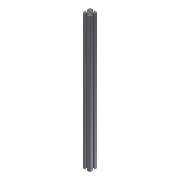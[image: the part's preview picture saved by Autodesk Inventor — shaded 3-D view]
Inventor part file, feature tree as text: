
AUTODESK INVENTOR PART (.ipt)
format: ipt  version: 2016 (Build 200138000, 138)  size: 182,784 bytes
history: native  units: mm
features: other x42, sketch x5, hole x4, extrude x1
ambient origin geometry x8: Origin, YZ Plane, XZ Plane, XY Plane, X Axis, Y Axis, Z Axis, Center Point
bodies: Solid1 (feature_tree)
feature tree (52):
  extrude  "Extrusion1"  [1 undecoded]
  hole  "Drilling 1"  [1 undecoded]
  hole  "Drilling 2"  [1 undecoded]
  hole  "Drilling 3"  [1 undecoded]
  hole  "Drilling 4"  [1 undecoded]
  other  "side_4d_XY"
  other  "side_4d_YZ"
  other  "side_4d_ZX"
  other  "side_4d_X"
  other  "side_4d_Y"
  other  "side_4d_Z"
  other  "side_4d_Center"
  other  "side_1a_XY"
  other  "side_1a_YZ"
  other  "side_1a_ZX"
  other  "side_1a_X"
  other  "side_1a_Y"
  other  "side_1a_Z"
  other  "side_1a_Center"
  other  "side_2b_XY"
  other  "side_2b_YZ"
  other  "side_2b_ZX"
  other  "side_2b_X"
  other  "side_2b_Y"
  other  "side_2b_Z"
  other  "side_2b_Center"
  other  "side_3c_XY"
  other  "side_3c_YZ"
  other  "side_3c_ZX"
  other  "side_3c_X"
  other  "side_3c_Y"
  other  "side_3c_Z"
  other  "side_3c_Center"
  other  "end_XY"
  other  "end_YZ"
  other  "end_ZX"
  other  "end_X"
  other  "end_Y"
  other  "end_Z"
  other  "end_Center"
  other  "start_XY"
  other  "start_YZ"
  other  "start_ZX"
  other  "start_X"
  other  "start_Y"
  other  "start_Z"
  other  "start_Center"
  sketch  "Skizze_1"  dims[d0=720.0mm d1=0.0mm]
  sketch  "Sketch2"  dims[d2=5.0mm d3=6.0mm d4=4.0mm d5=2.0mm d6=90.0deg d7=6000.0mm d8=0.0mm]
  sketch  "Sketch3"  dims[d9=5.0mm d10=6.0mm d11=4.0mm d12=2.0mm d13=90.0deg d14=6000.0mm d15=0.0mm]
  sketch  "Sketch4"  dims[d16=5.0mm d17=6.0mm d18=4.0mm d19=2.0mm d20=90.0deg d21=6000.0mm d22=0.0mm]
  sketch  "Sketch5"  dims[d23=5.0mm d24=6.0mm d25=4.0mm d26=2.0mm d27=90.0deg d28=6000.0mm d29=0.0mm]
note: 5 required parameter values undecoded (feature->parameter linkage not recoverable at this tier; creation-order binding heuristic only, values carry confidence <= 0.55)
